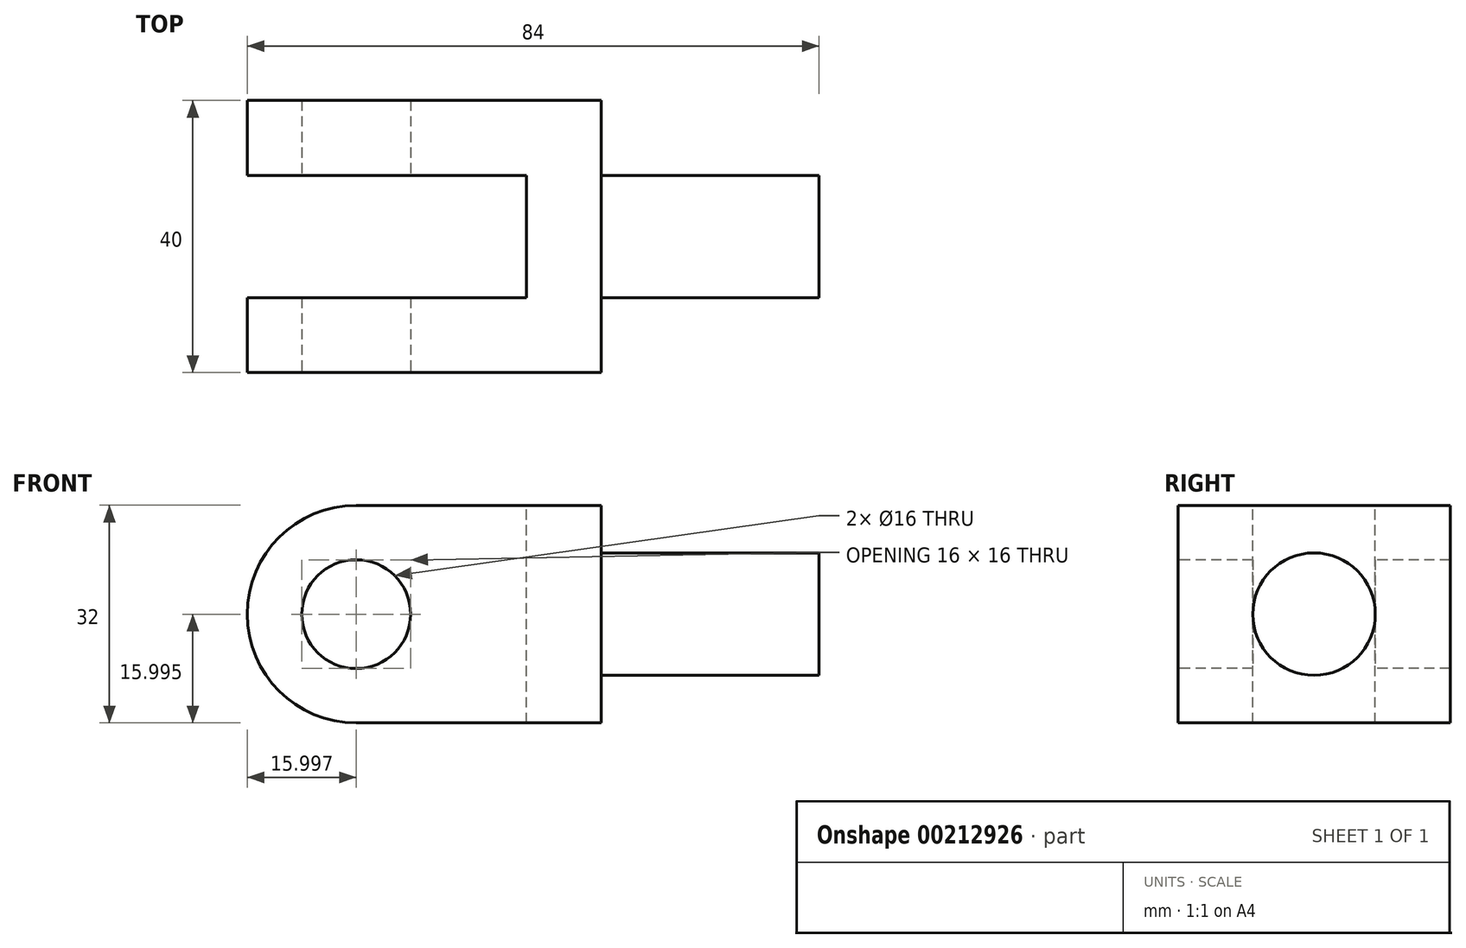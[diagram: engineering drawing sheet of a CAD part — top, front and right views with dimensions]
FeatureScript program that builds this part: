
annotation { "Feature Type Name" : "Feature", "Feature Type Description" : "" }
export const myFeature = defineFeature(function(context is Context, id is Id, definition is map)
    precondition{}
    {
        {
            var Q0;
            Q0=qCreatedBy(makeId("Front.planeOp"),FACE);
            var sketch = newSketch(context, id + "F0", { "sketchPlane" : qUnion([Q0])});
            skLineSegment(sketch, "E0.bottom", {"start": v(-19.64, 20.55) * mm, "end": v(32.36, 20.55) * mm});
            skLineSegment(sketch, "E0.top", {"start": v(-19.64, -11.45) * mm, "end": v(32.36, -11.45) * mm});
            skLineSegment(sketch, "E0.left", {"start": v(-19.64, 20.55) * mm, "end": v(-19.64, -11.45) * mm});
            skLineSegment(sketch, "E0.right", {"start": v(32.36, 20.55) * mm, "end": v(32.36, -11.45) * mm});
            skSolve(sketch);
        }
        {
            var Q0;
            Q0=makeQuery(id+"F0.imprint","IMPRINT",FACE,{"disambiguationData":[TD([[makeQuery(id+"F0.imprint","IMPRINT",EDGE,{"derivedFrom":sQuery(id+"F0.wireOp",EDGE,"E0.bottom")}),-1.0]])]});
            extrude(context, id + "F1", {"entities" : qUnion([Q0]), "depth" : 40 * mm});
        }
        {
            var Q0;
            Q0=makeQuery(id+"F1.opExtrude","SWEPT_EDGE",EDGE,{"disambiguationData":[OSD([sQuery(id+"F0.wireOp",EDGE,"E0.bottom"),sQuery(id+"F0.wireOp",EDGE,"E0.left")])]});
            var Q1;
            Q1=makeQuery(id+"F1.opExtrude","SWEPT_EDGE",EDGE,{"disambiguationData":[OSD([sQuery(id+"F0.wireOp",EDGE,"E0.top"),sQuery(id+"F0.wireOp",EDGE,"E0.left")])]});
            fillet(context, id + "F2", {"entities" : qUnion([Q0, Q1]), "radius" : 16 * mm, "tangentPropagation" : true, "allowEdgeOverflow" : false});
        }
        {
            var Q0;
            Q0=makeQuery(id+"F1.opExtrude","CAP_FACE",FACE,{"disambiguationData":[OSD([sQuery(id+"F0.wireOp",EDGE,"E0.bottom"),sQuery(id+"F0.wireOp",EDGE,"E0.top"),sQuery(id+"F0.wireOp",EDGE,"E0.left"),sQuery(id+"F0.wireOp",EDGE,"E0.right")])],"isStart":false});
            var sketch = newSketch(context, id + "F3", { "sketchPlane" : qUnion([Q0])});
            skCircle(sketch, "E1", {"center": v(-3.64, 4.55) * mm, "radius": 8 * mm});
            skSolve(sketch);
        }
        {
            var Q0;
            Q0=makeQuery(id+"F3.imprint","IMPRINT",FACE,{"disambiguationData":[TD([[makeQuery(id+"F3.imprint","IMPRINT",EDGE,{"derivedFrom":sQuery(id+"F3.wireOp",EDGE,"E1")}),1.0]])]});
            extrude(context, id + "F4", {"entities" : qUnion([Q0]), "operationType" : NewBodyOperationType.REMOVE, "endBound" : BoundingType.THROUGH_ALL, "oppositeDirection" : true, "depth" : 25 * mm});
        }
        {
            var Q0;
            Q0=makeQuery(id+"F1.opExtrude","SWEPT_FACE",FACE,{"disambiguationData":[OSD([sQuery(id+"F0.wireOp",EDGE,"E0.bottom")])]});
            var sketch = newSketch(context, id + "F5", { "sketchPlane" : qUnion([Q0])});
            skLineSegment(sketch, "E2", {"start": v(-44.97, -20) * mm, "end": v(32.36, -20) * mm, "construction": true});
            skPoint(sketch, "E2.startSnap0", {"position": v(32.36, -20) * mm});
            skLineSegment(sketch, "E3.bottom", {"start": v(21.36, -11) * mm, "end": v(-30.64, -11) * mm});
            skLineSegment(sketch, "E3.top", {"start": v(21.36, -29) * mm, "end": v(-30.64, -29) * mm});
            skLineSegment(sketch, "E3.left", {"start": v(21.36, -11) * mm, "end": v(21.36, -29) * mm});
            skLineSegment(sketch, "E3.right", {"start": v(-30.64, -11) * mm, "end": v(-30.64, -29) * mm});
            skSolve(sketch);
        }
        {
            var Q0;
            {var subQ0=sQuery(id+"F5.wireOp",EDGE,"E3.right");Q0=makeQuery(id+"F5.imprint","IMPRINT",FACE,{"disambiguationData":[TD([[makeQuery(id+"F5.imprint","IMPRINT",EDGE,{"derivedFrom":subQ0}),1.0]])]});}
            var Q1;
            {var subQ0=sQuery(id+"F5.wireOp",EDGE,"E3.left");Q1=makeQuery(id+"F5.imprint","IMPRINT",FACE,{"disambiguationData":[TD([[makeQuery(id+"F5.imprint","IMPRINT",EDGE,{"derivedFrom":subQ0}),-1.0]])]});}
            extrude(context, id + "F6", {"entities" : qUnion([Q0, Q1]), "operationType" : NewBodyOperationType.REMOVE, "endBound" : BoundingType.THROUGH_ALL, "oppositeDirection" : true, "depth" : 25 * mm});
        }
        {
            var Q0;
            Q0=makeQuery(id+"F1.opExtrude","SWEPT_FACE",FACE,{"disambiguationData":[OSD([sQuery(id+"F0.wireOp",EDGE,"E0.right")])]});
            var sketch = newSketch(context, id + "F7", { "sketchPlane" : qUnion([Q0])});
            skCircle(sketch, "E4", {"center": v(-20, 4.55) * mm, "radius": 9 * mm});
            skPoint(sketch, "E4.centerSnap0", {"position": v(0, 4.55) * mm});
            skPoint(sketch, "E4.centerSnap1", {"position": v(-20, 20.55) * mm});
            skSolve(sketch);
        }
        {
            var Q0;
            Q0=makeQuery(id+"F7.imprint","IMPRINT",FACE,{"disambiguationData":[TD([[makeQuery(id+"F7.imprint","IMPRINT",EDGE,{"derivedFrom":sQuery(id+"F7.wireOp",EDGE,"E4")}),1.0]])]});
            extrude(context, id + "F8", {"entities" : qUnion([Q0]), "operationType" : NewBodyOperationType.ADD, "depth" : 32 * mm});
        }
    });
